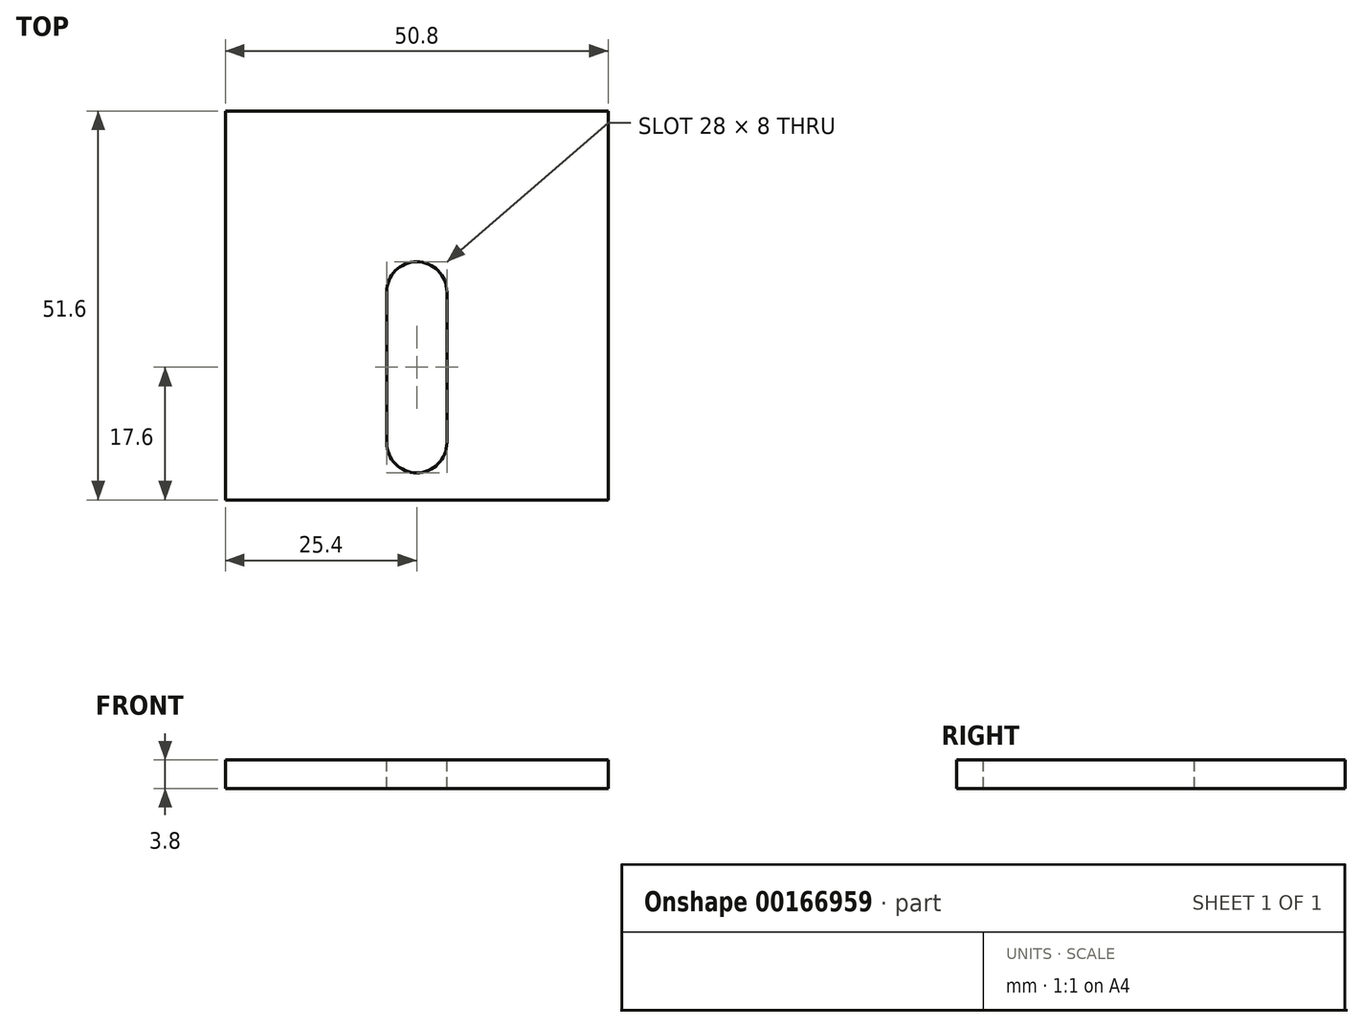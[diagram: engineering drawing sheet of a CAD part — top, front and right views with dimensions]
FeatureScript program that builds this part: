
annotation { "Feature Type Name" : "Feature", "Feature Type Description" : "" }
export const myFeature = defineFeature(function(context is Context, id is Id, definition is map)
    precondition{}
    {
        {
            var Q0;
            Q0=qCreatedBy(makeId("Top.planeOp"),FACE);
            var sketch = newSketch(context, id + "F0", { "sketchPlane" : qUnion([Q0])});
            skLineSegment(sketch, "E0.bottom", {"start": v(-25.4, 25.8) * mm, "end": v(25.4, 25.8) * mm});
            skLineSegment(sketch, "E0.top", {"start": v(-25.4, -25.8) * mm, "end": v(25.4, -25.8) * mm});
            skLineSegment(sketch, "E0.left", {"start": v(-25.4, 25.8) * mm, "end": v(-25.4, -25.8) * mm});
            skLineSegment(sketch, "E0.right", {"start": v(25.4, 25.8) * mm, "end": v(25.4, -25.8) * mm});
            skSolve(sketch);
        }
        {
            var Q0;
            Q0 = qSketchRegion(id + "F0", true);
            extrude(context, id + "F1", {"entities" : qUnion([Q0]), "depth" : 3.8 * mm});
        }
        {
            var Q0;
            Q0=makeQuery(id+"F1.opExtrude","CAP_FACE",FACE,{"disambiguationData":[OSD([sQuery(id+"F0.wireOp",EDGE,"E0.bottom"),sQuery(id+"F0.wireOp",EDGE,"E0.top"),sQuery(id+"F0.wireOp",EDGE,"E0.left"),sQuery(id+"F0.wireOp",EDGE,"E0.right")])],"isStart":false});
            var sketch = newSketch(context, id + "F2", { "sketchPlane" : qUnion([Q0])});
            skArc(sketch, "E1", {"start": v(4, 1.8) * mm, "mid": v(0, 5.8) * mm, "end": v(-4, 1.8) * mm});
            skArc(sketch, "E2", {"start": v(-4, -18.2) * mm, "mid": v(0, -22.2) * mm, "end": v(4, -18.2) * mm});
            skLineSegment(sketch, "E3", {"start": v(-4, 1.8) * mm, "end": v(-4, -18.2) * mm});
            skLineSegment(sketch, "E4", {"start": v(4, 1.8) * mm, "end": v(4, -18.2) * mm});
            skSolve(sketch);
        }
        {
            var Q0;
            Q0 = qSketchRegion(id + "F2", true);
            extrude(context, id + "F3", {"entities" : qUnion([Q0]), "operationType" : NewBodyOperationType.REMOVE, "endBound" : BoundingType.THROUGH_ALL, "oppositeDirection" : true, "depth" : 25 * mm});
        }
    });
